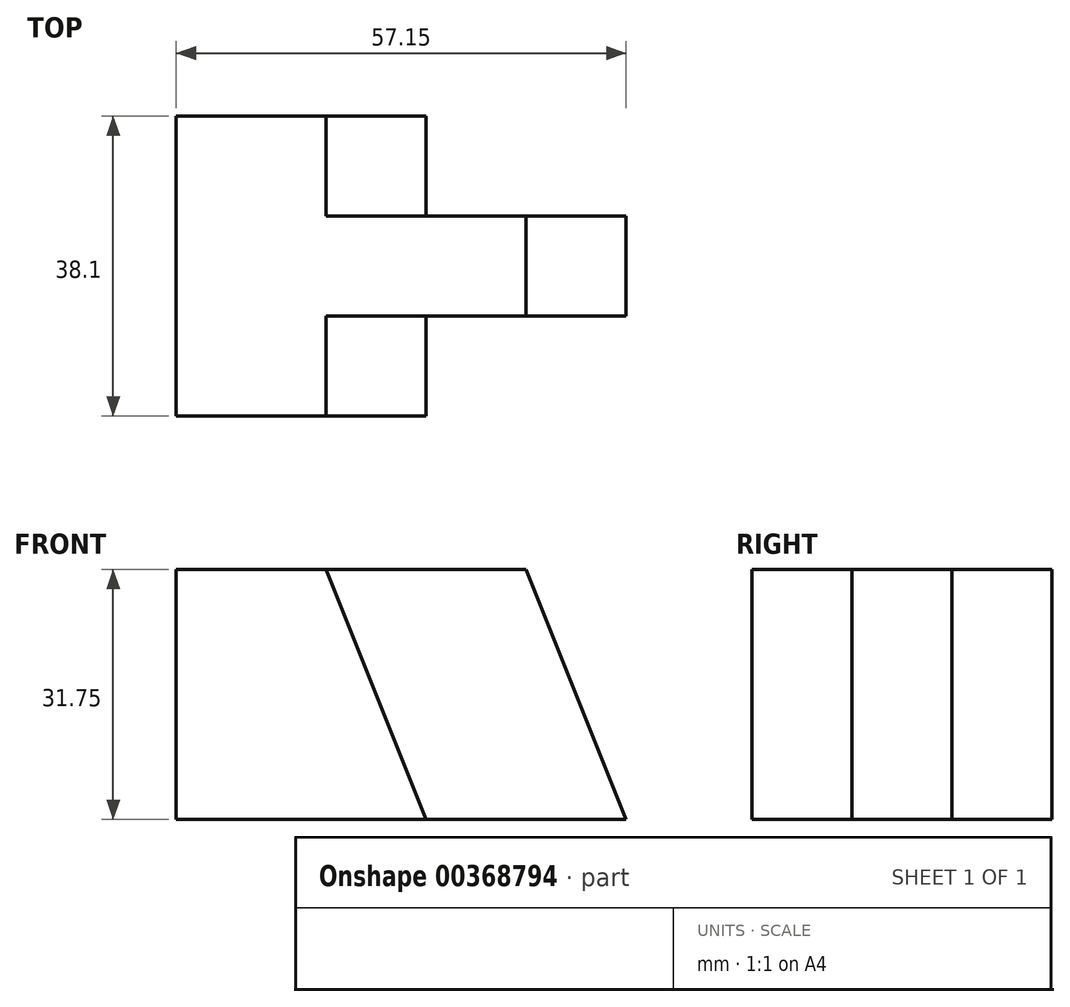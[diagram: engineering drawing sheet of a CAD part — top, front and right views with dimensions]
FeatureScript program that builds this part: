
annotation { "Feature Type Name" : "Feature", "Feature Type Description" : "" }
export const myFeature = defineFeature(function(context is Context, id is Id, definition is map)
    precondition{}
    {
        {
            var Q0;
            Q0=qCreatedBy(makeId("Front.planeOp"),FACE);
            var sketch = newSketch(context, id + "F0", { "sketchPlane" : qUnion([Q0])});
            skLineSegment(sketch, "E0.bottom", {"start": v(0, 0) * mm, "end": v(57.15, 0) * mm});
            skLineSegment(sketch, "E0.top", {"start": v(0, 31.75) * mm, "end": v(57.15, 31.75) * mm});
            skLineSegment(sketch, "E0.left", {"start": v(0, 0) * mm, "end": v(0, 31.75) * mm});
            skLineSegment(sketch, "E0.right", {"start": v(57.15, 0) * mm, "end": v(57.15, 31.75) * mm});
            skSolve(sketch);
        }
        {
            var Q0;
            Q0 = qSketchRegion(id + "F0", true);
            extrude(context, id + "F1", {"entities" : qUnion([Q0]), "depth" : 25.4 * mm});
        }
        {
            var Q0;
            Q0=makeQuery(id+"F1.opExtrude","CAP_FACE",FACE,{"disambiguationData":[OSD([sQuery(id+"F0.wireOp",EDGE,"E0.bottom"),sQuery(id+"F0.wireOp",EDGE,"E0.top"),sQuery(id+"F0.wireOp",EDGE,"E0.left"),sQuery(id+"F0.wireOp",EDGE,"E0.right")])],"isStart":false});
            var sketch = newSketch(context, id + "F2", { "sketchPlane" : qUnion([Q0])});
            skLineSegment(sketch, "E1", {"start": v(31.75, 0) * mm, "end": v(19.05, 31.75) * mm});
            skSolve(sketch);
        }
        {
            var Q0;
            {var subQ0=sQuery(id+"F2.wireOp",EDGE,"E1");Q0=makeQuery(id+"F2.imprint","IMPRINT",FACE,{"disambiguationData":[TD([[makeQuery(id+"F2.imprint","IMPRINT",EDGE,{"derivedFrom":subQ0}),-1.0]])]});}
            extrude(context, id + "F3", {"entities" : qUnion([Q0]), "operationType" : NewBodyOperationType.REMOVE, "oppositeDirection" : true, "depth" : 12.7 * mm});
        }
        {
            var Q0;
            Q0=makeQuery(id+"F1.opExtrude","CAP_FACE",FACE,{"disambiguationData":[OSD([sQuery(id+"F0.wireOp",EDGE,"E0.bottom"),sQuery(id+"F0.wireOp",EDGE,"E0.top"),sQuery(id+"F0.wireOp",EDGE,"E0.left"),sQuery(id+"F0.wireOp",EDGE,"E0.right")])],"isStart":true});
            extrude(context, id + "F4", {"entities" : qUnion([Q0]), "operationType" : NewBodyOperationType.ADD, "depth" : 12.7 * mm});
        }
        {
            var Q0;
            Q0=makeQuery(id+"F4.opExtrude","CAP_FACE",FACE,{"disambiguationData":[OSD([sQuery(id+"F0.wireOp",EDGE,"E0.bottom"),sQuery(id+"F0.wireOp",EDGE,"E0.top"),sQuery(id+"F0.wireOp",EDGE,"E0.left"),sQuery(id+"F0.wireOp",EDGE,"E0.right")])],"isStart":false});
            var sketch = newSketch(context, id + "F5", { "sketchPlane" : qUnion([Q0])});
            skLineSegment(sketch, "E2", {"start": v(-19.05, 31.75) * mm, "end": v(-31.75, 0) * mm});
            skSolve(sketch);
        }
        {
            var Q0;
            {var subQ0=sQuery(id+"F5.wireOp",EDGE,"E2");Q0=makeQuery(id+"F5.imprint","IMPRINT",FACE,{"disambiguationData":[TD([[makeQuery(id+"F5.imprint","IMPRINT",EDGE,{"derivedFrom":subQ0}),-1.0]])]});}
            extrude(context, id + "F6", {"entities" : qUnion([Q0]), "operationType" : NewBodyOperationType.REMOVE, "oppositeDirection" : true, "depth" : 12.7 * mm});
        }
        {
            var Q0;
            Q0=makeQuery(id+"F6.boolean.opBoolean","COPY",FACE,{"derivedFrom":makeQuery(id+"F6.opExtrude","CAP_FACE",FACE,{"disambiguationData":[OSD([sQuery(id+"F0.wireOp",EDGE,"E0.bottom"),sQuery(id+"F0.wireOp",EDGE,"E0.top"),sQuery(id+"F0.wireOp",EDGE,"E0.right"),sQuery(id+"F5.wireOp",EDGE,"E2")])],"isStart":false})});
            var sketch = newSketch(context, id + "F7", { "sketchPlane" : qUnion([Q0])});
            skLineSegment(sketch, "E3", {"start": v(-57.15, 0) * mm, "end": v(-44.45, 31.75) * mm});
            skSolve(sketch);
        }
        {
            var Q0;
            {var subQ0=sQuery(id+"F7.wireOp",EDGE,"E3");Q0=makeQuery(id+"F7.imprint","IMPRINT",FACE,{"disambiguationData":[TD([[makeQuery(id+"F7.imprint","IMPRINT",EDGE,{"derivedFrom":subQ0}),1.0]])]});}
            extrude(context, id + "F8", {"entities" : qUnion([Q0]), "operationType" : NewBodyOperationType.REMOVE, "oppositeDirection" : true, "depth" : 12.7 * mm});
        }
    });
